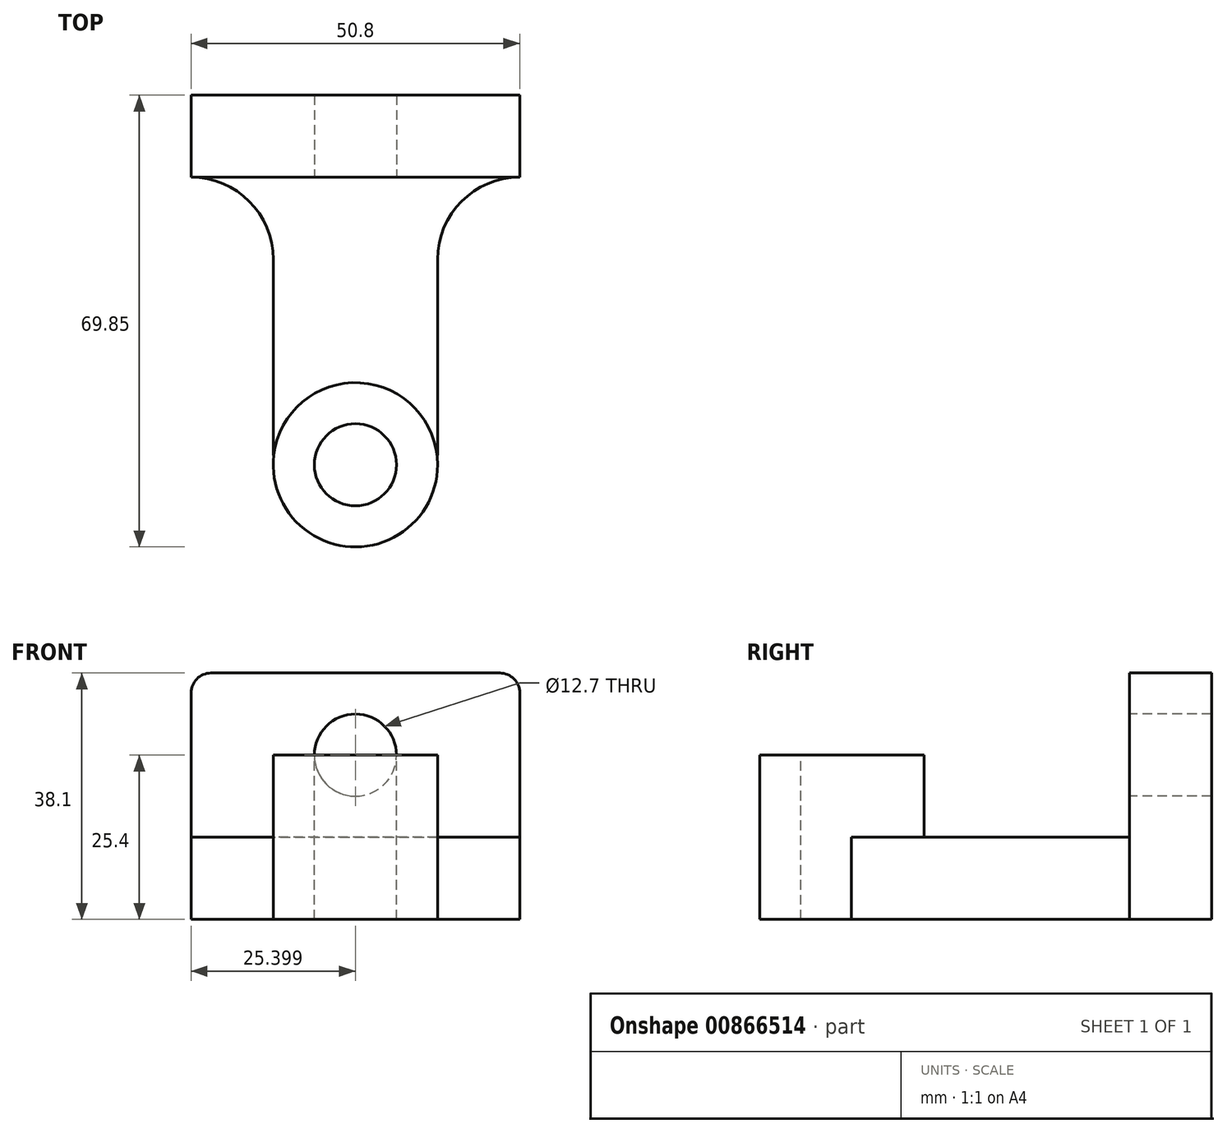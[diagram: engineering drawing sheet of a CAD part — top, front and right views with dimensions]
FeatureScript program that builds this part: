
annotation { "Feature Type Name" : "Feature", "Feature Type Description" : "" }
export const myFeature = defineFeature(function(context is Context, id is Id, definition is map)
    precondition{}
    {
        {
            var Q0;
            Q0=qCreatedBy(makeId("Top.planeOp"),FACE);
            var sketch = newSketch(context, id + "F0", { "sketchPlane" : qUnion([Q0])});
            skLineSegment(sketch, "E0.bottom", {"start": v(-59.86, 0) * mm, "end": v(-9.06, 0) * mm});
            skLineSegment(sketch, "E0.top", {"start": v(-59.86, -12.7) * mm, "end": v(-9.06, -12.7) * mm});
            skLineSegment(sketch, "E0.left", {"start": v(-59.86, 0) * mm, "end": v(-59.86, -12.7) * mm});
            skLineSegment(sketch, "E0.right", {"start": v(-9.06, 0) * mm, "end": v(-9.06, -12.7) * mm});
            skSolve(sketch);
        }
        {
            var Q0;
            Q0 = qSketchRegion(id + "F0", true);
            extrude(context, id + "F1", {"entities" : qUnion([Q0]), "depth" : 38.1 * mm, "offsetDistance" : 25.4 * mm});
        }
        {
            var Q0;
            Q0=makeQuery(id+"F1.opExtrude","CAP_FACE",FACE,{"disambiguationData":[OSD([sQuery(id+"F0.wireOp",EDGE,"E0.bottom"),sQuery(id+"F0.wireOp",EDGE,"E0.top"),sQuery(id+"F0.wireOp",EDGE,"E0.left"),sQuery(id+"F0.wireOp",EDGE,"E0.right")])],"isStart":true});
            var sketch = newSketch(context, id + "F2", { "sketchPlane" : qUnion([Q0])});
            skLineSegment(sketch, "E1.bottom", {"start": v(-59.86, 12.7) * mm, "end": v(-9.06, 12.7) * mm});
            skArc(sketch, "E2", {"start": v(-59.86, 12.7) * mm, "mid": v(-50.88, 16.42) * mm, "end": v(-47.16, 25.4) * mm});
            skArc(sketch, "E3", {"start": v(-21.76, 25.4) * mm, "mid": v(-18.04, 16.42) * mm, "end": v(-9.06, 12.7) * mm});
            skLineSegment(sketch, "E4.bottom", {"start": v(-47.16, 25.4) * mm, "end": v(-21.76, 25.4) * mm});
            skLineSegment(sketch, "E4.top", {"start": v(-47.16, 49.35) * mm, "end": v(-21.76, 49.35) * mm});
            skLineSegment(sketch, "E4.left", {"start": v(-47.16, 25.4) * mm, "end": v(-47.16, 49.35) * mm});
            skLineSegment(sketch, "E4.right", {"start": v(-21.76, 25.4) * mm, "end": v(-21.76, 49.35) * mm});
            skSolve(sketch);
        }
        {
            var Q0;
            Q0 = qSketchRegion(id + "F2", true);
            extrude(context, id + "F3", {"entities" : qUnion([Q0]), "operationType" : NewBodyOperationType.ADD, "oppositeDirection" : true, "depth" : 12.7 * mm, "offsetDistance" : 25.4 * mm});
        }
        {
            var Q0;
            Q0=makeQuery(id+"F3.opExtrude","CAP_FACE",FACE,{"disambiguationData":[OSD([sQuery(id+"F2.wireOp",EDGE,"E1.bottom"),sQuery(id+"F2.wireOp",EDGE,"E2"),sQuery(id+"F2.wireOp",EDGE,"E3"),sQuery(id+"F2.wireOp",EDGE,"E4.top"),sQuery(id+"F2.wireOp",EDGE,"E4.left"),sQuery(id+"F2.wireOp",EDGE,"E4.right")])],"isStart":false});
            var sketch = newSketch(context, id + "F4", { "sketchPlane" : qUnion([Q0])});
            skCircle(sketch, "E5", {"center": v(-34.46, -57.15) * mm, "radius": 12.7 * mm});
            skSolve(sketch);
        }
        {
            var Q0;
            {var subQ0=sQuery(id+"F4.wireOp",EDGE,"E5");var subQ1=makeQuery(id+"F3.opExtrude","CAP_EDGE",EDGE,{"disambiguationData":[OSD([sQuery(id+"F2.wireOp",EDGE,"E4.top")])],"isStart":false});var subQ2=makeQuery(id+"F4.imprint","INTERSECT",VERTEX,{"disambiguationData":[OD(0.0)],"derivedFrom":[subQ1,subQ0]});Q0=makeQuery(id+"F4.imprint","IMPRINT",FACE,{"disambiguationData":[TD([[makeQuery(id+"F4.imprint","IMPRINT",EDGE,{"disambiguationData":[TD([[subQ2,1.0]])],"derivedFrom":subQ0}),1.0]])]});}
            var Q1;
            {var subQ0=sQuery(id+"F4.wireOp",EDGE,"E5");var subQ1=makeQuery(id+"F3.opExtrude","CAP_EDGE",EDGE,{"disambiguationData":[OSD([sQuery(id+"F2.wireOp",EDGE,"E4.top")])],"isStart":false});var subQ2=makeQuery(id+"F4.imprint","INTERSECT",VERTEX,{"disambiguationData":[OD(0.0)],"derivedFrom":[subQ1,subQ0]});Q1=makeQuery(id+"F4.imprint","IMPRINT",FACE,{"disambiguationData":[TD([[makeQuery(id+"F4.imprint","IMPRINT",EDGE,{"disambiguationData":[TD([[subQ2,-1.0]])],"derivedFrom":subQ0}),1.0]])]});}
            var Q2;
            Q2=sQuery(id+"F4.wireOp",EDGE,"E5");
            extrude(context, id + "F5", {"entities" : qUnion([Q0, Q1]), "operationType" : NewBodyOperationType.ADD, "surfaceEntities" : qUnion([Q2]), "depth" : 12.7 * mm, "offsetDistance" : 25.4 * mm});
        }
        {
            var Q0;
            Q0=makeQuery(id+"F5.opExtrude","CAP_FACE",FACE,{"disambiguationData":[OSD([sQuery(id+"F4.wireOp",EDGE,"E5")])],"isStart":false});
            extrude(context, id + "F6", {"entities" : qUnion([Q0]), "operationType" : NewBodyOperationType.ADD, "oppositeDirection" : true, "depth" : 25.4 * mm, "offsetDistance" : 25.4 * mm});
        }
        {
            var Q0;
            {var subQ1=sQuery(id+"F2.wireOp",EDGE,"E4.left");var subQ2=sQuery(id+"F2.wireOp",EDGE,"E4.top");Q0=makeQuery(id+"F6.boolean.opBoolean","SPLIT",FACE,{"disambiguationData":[TD([makeQuery(id+"F3.opExtrude","SWEPT_FACE",FACE,{"disambiguationData":[OSD([subQ1])]})])],"derivedFrom":makeQuery(id+"F3.opExtrude","SWEPT_FACE",FACE,{"disambiguationData":[OSD([subQ2])]})});}
            var Q1;
            {var subQ0=sQuery(id+"F2.wireOp",EDGE,"E4.right");var subQ2=sQuery(id+"F2.wireOp",EDGE,"E4.top");Q1=makeQuery(id+"F6.boolean.opBoolean","SPLIT",FACE,{"disambiguationData":[TD([makeQuery(id+"F3.opExtrude","SWEPT_FACE",FACE,{"disambiguationData":[OSD([subQ0])]})])],"derivedFrom":makeQuery(id+"F3.opExtrude","SWEPT_FACE",FACE,{"disambiguationData":[OSD([subQ2])]})});}
            extrude(context, id + "F7", {"entities" : qUnion([Q0, Q1]), "operationType" : NewBodyOperationType.ADD, "depth" : 6.35 * mm, "offsetDistance" : 25.4 * mm});
        }
        {
            var Q0;
            Q0=makeQuery(id+"F5.opExtrude","CAP_FACE",FACE,{"disambiguationData":[OSD([sQuery(id+"F4.wireOp",EDGE,"E5")])],"isStart":false});
            var sketch = newSketch(context, id + "F8", { "sketchPlane" : qUnion([Q0])});
            skCircle(sketch, "E6", {"center": v(-34.46, -57.15) * mm, "radius": 6.35 * mm});
            skSolve(sketch);
        }
        {
            var Q0;
            Q0=makeQuery(id+"F8.imprint","IMPRINT",FACE,{"disambiguationData":[TD([[makeQuery(id+"F8.imprint","IMPRINT",EDGE,{"derivedFrom":sQuery(id+"F8.wireOp",EDGE,"E6")}),1.0]])]});
            var Q1;
            Q1=sQuery(id+"F8.wireOp",EDGE,"E6");
            extrude(context, id + "F9", {"entities" : qUnion([Q0]), "operationType" : NewBodyOperationType.REMOVE, "surfaceEntities" : qUnion([Q1]), "oppositeDirection" : true, "depth" : 25.4 * mm, "offsetDistance" : 25.4 * mm});
        }
        {
            var Q0;
            Q0=makeQuery(id+"F1.opExtrude","SWEPT_FACE",FACE,{"disambiguationData":[OSD([sQuery(id+"F0.wireOp",EDGE,"E0.top")])]});
            var sketch = newSketch(context, id + "F10", { "sketchPlane" : qUnion([Q0])});
            skCircle(sketch, "E7", {"center": v(-34.46, 25.4) * mm, "radius": 6.35 * mm});
            skSolve(sketch);
        }
        {
            var Q0;
            Q0=makeQuery(id+"F10.imprint","IMPRINT",FACE,{"disambiguationData":[TD([[makeQuery(id+"F10.imprint","IMPRINT",EDGE,{"derivedFrom":sQuery(id+"F10.wireOp",EDGE,"E7")}),1.0]])]});
            var Q1;
            Q1=sQuery(id+"F10.wireOp",EDGE,"E7");
            extrude(context, id + "F11", {"entities" : qUnion([Q0]), "operationType" : NewBodyOperationType.REMOVE, "surfaceEntities" : qUnion([Q1]), "oppositeDirection" : true, "depth" : 25.4 * mm, "offsetDistance" : 25.4 * mm});
        }
        {
            var Q0;
            Q0=makeQuery(id+"F1.opExtrude","CAP_EDGE",EDGE,{"disambiguationData":[OSD([sQuery(id+"F0.wireOp",EDGE,"E0.left")])],"isStart":false});
            var Q1;
            Q1=makeQuery(id+"F1.opExtrude","CAP_EDGE",EDGE,{"disambiguationData":[OSD([sQuery(id+"F0.wireOp",EDGE,"E0.right")])],"isStart":false});
            fillet(context, id + "F12", {"entities" : qUnion([Q0, Q1]), "radius" : 3.07 * mm, "tangentPropagation" : true, "allowEdgeOverflow" : false});
        }
    });
